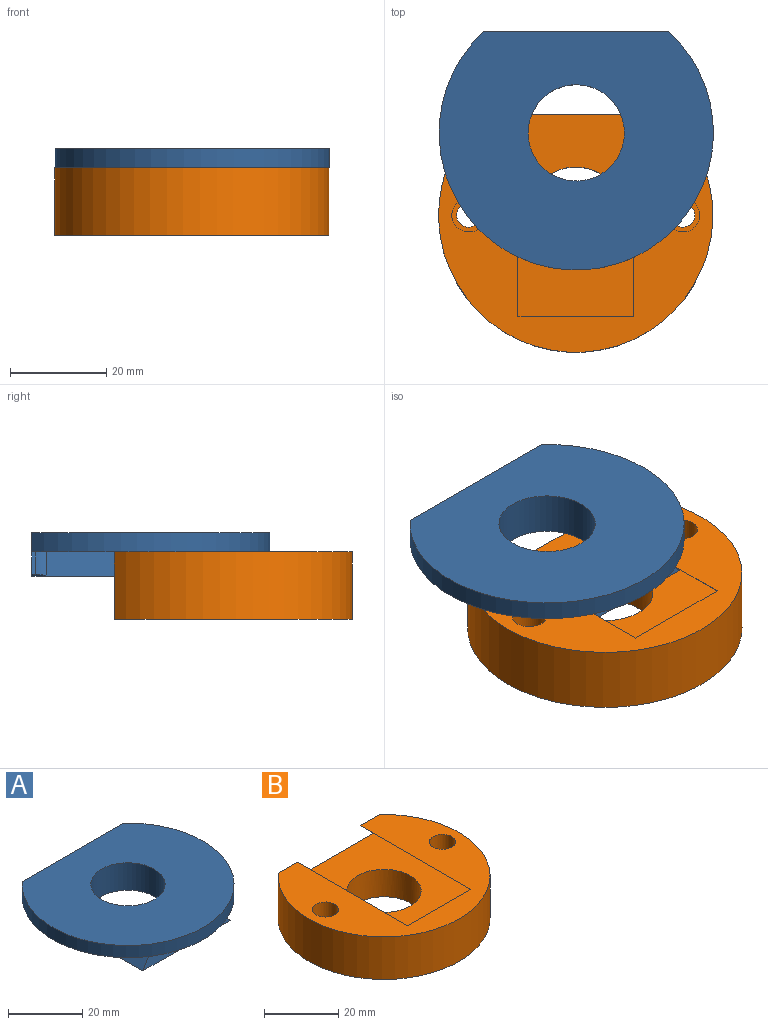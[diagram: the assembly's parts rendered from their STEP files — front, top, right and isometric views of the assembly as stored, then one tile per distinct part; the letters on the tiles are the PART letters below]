
ASSEMBLY  parts=2 mates=1
PART A: 15 faces, bbox 57x49.5x9 mm
  f0: plane 57x49.5mm, normal (0,0,-1), area 1371.8mm2, adj f1,f2,f6,f7,f8,f9,f11,f12
  f1: plane 38.54x9mm, normal (0,1,0), area 302.4mm2, adj f0,f2,f4,f5,f9,f10,f12,f13
  f2: cylinder r=28.5mm len=57mm, axis (0,0,-1), area 547mm2, adj f0,f1,f4
  f3: cylinder r=10mm len=20mm, axis (0,0,-1), area 565.5mm2, adj f4,f5
  f4: plane 57x49.5mm, normal (0,0,1), area 2039.2mm2, adj f1,f2,f3
  f5: plane 43.34x33.29mm, normal (0,0,-1), area 1128.7mm2, adj f1,f3,f6,f7,f8,f10,f13
  f6: plane 40.34x5mm, normal (-0.71,0,0.71), area 280.5mm2, adj f0,f5,f8,f11
  f7: plane 40.34x5mm, normal (0.71,0,0.71), area 280.5mm2, adj f0,f5,f8,f14
  f8: plane 33.29x5mm, normal (0,-0.97,0.26), area 146.5mm2, adj f0,f5,f6,f7
  f9: plane 4.65x4.65mm, normal (-0.71,0,0.71), area 5.4mm2, adj f0,f1,f10,f11
  f10: plane 3x0.35mm, normal (-0.71,0,-0.71), area 1.1mm2, adj f1,f5,f9,f11
  f11: cylinder r=5mm len=5.35mm, axis (0.71,0,0.71), area 15.2mm2, adj f0,f6,f9,f10
  f12: plane 4.65x4.65mm, normal (0.71,0,0.71), area 5.4mm2, adj f0,f1,f13,f14
  f13: plane 3x0.35mm, normal (0.71,0,-0.71), area 1.1mm2, adj f1,f5,f12,f14
  f14: cylinder r=5mm len=5.35mm, axis (0.71,0,-0.71), area 15.2mm2, adj f0,f7,f12,f13
PART B: 15 faces, bbox 57x49.5x14 mm
  f0: plane 57x49.5mm, normal (0,0,1), area 1268.4mm2, adj f3,f6,f7,f9,f12,f13,f14
  f1: cylinder r=2.5mm len=5mm, axis (0,0,-1), area 70.7mm2, adj f4,f10
  f2: cylinder r=2.5mm len=5mm, axis (0,0,-1), area 70.7mm2, adj f4,f8
  f3: cylinder r=28.5mm len=57mm, axis (0,0,-1), area 1914.5mm2, adj f0,f4,f6
  f4: plane 57x49.5mm, normal (0,0,-1), area 1999.9mm2, adj f1,f2,f3,f5,f6
  f5: cylinder r=10mm len=20mm, axis (0,0,-1), area 565.5mm2, adj f4,f11
  f6: plane 38.54x14mm, normal (0,1,0), area 394.5mm2, adj f0,f3,f4,f11,f12,f13
  f7: cylinder r=3.5mm len=9.5mm, axis (0,0,1), area 208.9mm2, adj f0,f8
  f8: plane 7x7mm, normal (0,0,1), area 18.8mm2, adj f2,f7
  f9: cylinder r=3.5mm len=9.5mm, axis (0,0,1), area 208.9mm2, adj f0,f10
  f10: plane 7x7mm, normal (0,0,1), area 18.8mm2, adj f1,f9
  f11: plane 43.34x34mm, normal (0,0,1), area 1159.4mm2, adj f5,f6,f12,f13,f14
  f12: plane 43.34x5mm, normal (0.71,0,-0.71), area 301.7mm2, adj f0,f6,f11,f14
  f13: plane 43.34x5mm, normal (-0.71,0,-0.71), area 301.7mm2, adj f0,f6,f11,f14
  f14: plane 34x5mm, normal (0,0.97,-0.26), area 150.1mm2, adj f0,f11,f12,f13
PLACE A t=(19.52,186.35,-23.12)mm
PLACE B t=(19.42,169.28,-23.12)mm
MATE slider A.f1 <-> B.f6  axis (0,1,0) through (36.17,207.35,-14.12)mm
